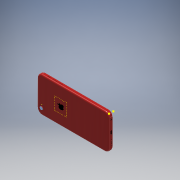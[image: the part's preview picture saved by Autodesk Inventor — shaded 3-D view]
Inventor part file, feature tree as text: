
AUTODESK INVENTOR PART (.ipt)
format: ipt  version: 2018 (Build 220112000, 112)  size: 498,176 bytes
history: native  units: mm
features: sketch x18, extrude x13, fillet x2, other x2
ambient origin geometry x8: Origin, YZ Plane, XZ Plane, XY Plane, X Axis, Y Axis, Z Axis, Center Point
bodies: Solid1 (feature_tree)
feature tree (35):
  extrude  "Extrusion1"  Depth=67.0mm
  fillet  "Fillet3"  Radius=8.0mm
  fillet  "Fillet4"  Radius=9.0mm
  sketch  "Sketch9"  dims[d14=2.5mm d21=9.5mm]
  extrude  "Extrusion2"  Depth=2.5mm
  sketch  "Sketch12"  dims[d64=0.6mm d65=0.0mm d67=0.7mm]
  extrude  "Extrusion5"  Depth=0.3mm TaperAngle=0.0deg
  sketch  "Sketch16"  dims[d71=0.5mm d72=0.5mm d73=0.0mm]
  extrude  "Extrusion6"  Depth=0.7mm
  extrude  "Extrusion7"  Depth=4.0mm TaperAngle=0.0deg
  extrude  "Extrusion8"  Depth=0.5mm TaperAngle=0.0deg
  extrude  "Extrusion9"  Depth=0.7mm TaperAngle=0.0deg
  extrude  "Extrusion10"  Depth=0.1mm
  sketch  "Sketch22"  dims[d90=0.3mm d91=0.0mm d92=0.3mm d93=0.0mm]
  extrude  "Extrusion11"  Depth=0.5mm
  extrude  "Extrusion12"  Depth=1.0mm TaperAngle=0.0deg
  extrude  "Extrusion13"  Depth=0.3mm TaperAngle=0.0deg
  extrude  "Extrusion14"  Depth=0.3mm TaperAngle=0.0deg
  extrude  "Extrusion15"  [1 undecoded]
  sketch  "Sketch28"
  sketch  "Sketch1"  dims[d0=138.0mm d1=67.0mm d2=8.0mm d3=0.0mm d13=9.0mm]
  sketch  "Sketch11"  dims[d22=1.0mm d36=0.3mm d37=0.0mm]
  other  "Image2"
  sketch  "Sketch15"  dims[d68=0.7mm d69=4.0mm d70=0.0mm]
  sketch  "Sketch17"  dims[d74=0.3mm d75=0.7mm d76=0.0mm]
  sketch  "Sketch18"  dims[d77=0.1mm d78=0.1mm]
  sketch  "Sketch19"  dims[d79=0.9mm d80=0.0mm d81=0.5mm]
  sketch  "Sketch20"  dims[d82=0.5mm d83=0.0mm d84=1.0mm d85=0.0mm]
  sketch  "Sketch21"  dims[d86=0.3mm d87=0.0mm d88=0.3mm d89=0.0mm]
  sketch  "Sketch23"
  sketch  "Sketch24"
  sketch  "Sketch25"
  sketch  "Sketch26"
  sketch  "Sketch27"
  other  "Image3"
note: 1 required parameter value undecoded (feature->parameter linkage not recoverable at this tier; creation-order binding heuristic only, values carry confidence <= 0.55)
